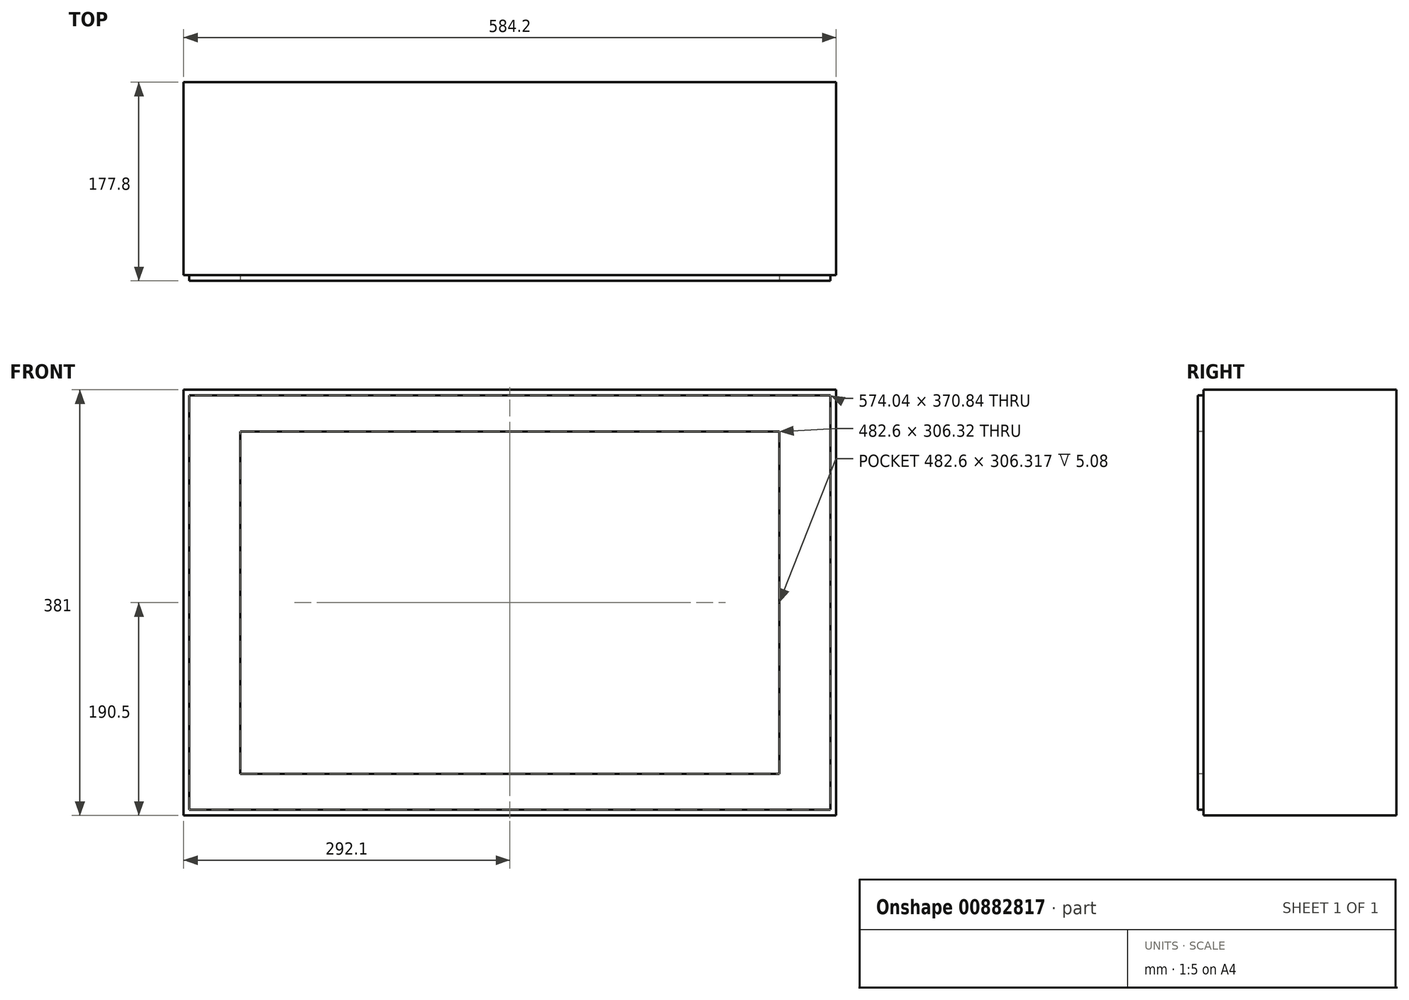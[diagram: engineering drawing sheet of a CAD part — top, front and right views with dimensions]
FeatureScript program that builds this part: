
annotation { "Feature Type Name" : "Feature", "Feature Type Description" : "" }
export const myFeature = defineFeature(function(context is Context, id is Id, definition is map)
    precondition{}
    {
        {
            var Q0;
            Q0=qCreatedBy(makeId("Front.planeOp"),FACE);
            var sketch = newSketch(context, id + "F0", { "sketchPlane" : qUnion([Q0])});
            skLineSegment(sketch, "E0.bottom", {"start": v(292.1, 190.5) * mm, "end": v(-292.1, 190.5) * mm});
            skLineSegment(sketch, "E0.top", {"start": v(292.1, -190.5) * mm, "end": v(-292.1, -190.5) * mm});
            skLineSegment(sketch, "E0.left", {"start": v(292.1, 190.5) * mm, "end": v(292.1, -190.5) * mm});
            skLineSegment(sketch, "E0.right", {"start": v(-292.1, 190.5) * mm, "end": v(-292.1, -190.5) * mm});
            skPoint(sketch, "E0.middle", {"position": v(0, 0) * mm});
            skSolve(sketch);
        }
        {
            var Q0;
            Q0 = qSketchRegion(id + "F0", true);
            extrude(context, id + "F1", {"entities" : qUnion([Q0]), "depth" : 177.8 * mm, "offsetDistance" : 25.4 * mm});
        }
        {
            var Q0;
            Q0=makeQuery(id+"F1.opExtrude","CAP_FACE",FACE,{"disambiguationData":[OSD([sQuery(id+"F0.wireOp",EDGE,"E0.bottom"),sQuery(id+"F0.wireOp",EDGE,"E0.top"),sQuery(id+"F0.wireOp",EDGE,"E0.left"),sQuery(id+"F0.wireOp",EDGE,"E0.right")])],"isStart":false});
            var sketch = newSketch(context, id + "F2", { "sketchPlane" : qUnion([Q0])});
            skLineSegment(sketch, "E1.bottom", {"start": v(241.3, 153.16) * mm, "end": v(-241.3, 153.16) * mm});
            skLineSegment(sketch, "E1.top", {"start": v(241.3, -153.16) * mm, "end": v(-241.3, -153.16) * mm});
            skLineSegment(sketch, "E1.left", {"start": v(241.3, 153.16) * mm, "end": v(241.3, -153.16) * mm});
            skLineSegment(sketch, "E1.right", {"start": v(-241.3, 153.16) * mm, "end": v(-241.3, -153.16) * mm});
            skPoint(sketch, "E1.middle", {"position": v(0, 0) * mm});
            skLineSegment(sketch, "E2.bottom", {"start": v(287.02, -185.42) * mm, "end": v(-287.02, -185.42) * mm});
            skLineSegment(sketch, "E2.top", {"start": v(287.02, 185.42) * mm, "end": v(-287.02, 185.42) * mm});
            skLineSegment(sketch, "E2.left", {"start": v(287.02, -185.42) * mm, "end": v(287.02, 185.42) * mm});
            skLineSegment(sketch, "E2.right", {"start": v(-287.02, -185.42) * mm, "end": v(-287.02, 185.42) * mm});
            skLineSegment(sketch, "E3.bottom", {"start": v(-292.1, 190.5) * mm, "end": v(292.1, 190.5) * mm});
            skLineSegment(sketch, "E3.top", {"start": v(-292.1, -190.5) * mm, "end": v(292.1, -190.5) * mm});
            skLineSegment(sketch, "E3.left", {"start": v(-292.1, 190.5) * mm, "end": v(-292.1, -190.5) * mm});
            skLineSegment(sketch, "E3.right", {"start": v(292.1, 190.5) * mm, "end": v(292.1, -190.5) * mm});
            skSolve(sketch);
        }
        {
            var Q0;
            Q0 = qSketchRegion(id + "F2", true);
            var Q1;
            Q1=makeQuery(id+"F2.imprint","IMPRINT",FACE,{"disambiguationData":[TD([[makeQuery(id+"F2.imprint","IMPRINT",EDGE,{"derivedFrom":sQuery(id+"F2.wireOp",EDGE,"E1.bottom")}),1.0]])]});
            extrude(context, id + "F3", {"entities" : qUnion([Q0, Q1]), "operationType" : NewBodyOperationType.REMOVE, "oppositeDirection" : true, "depth" : 5.08 * mm, "offsetDistance" : 25.4 * mm});
        }
    });
